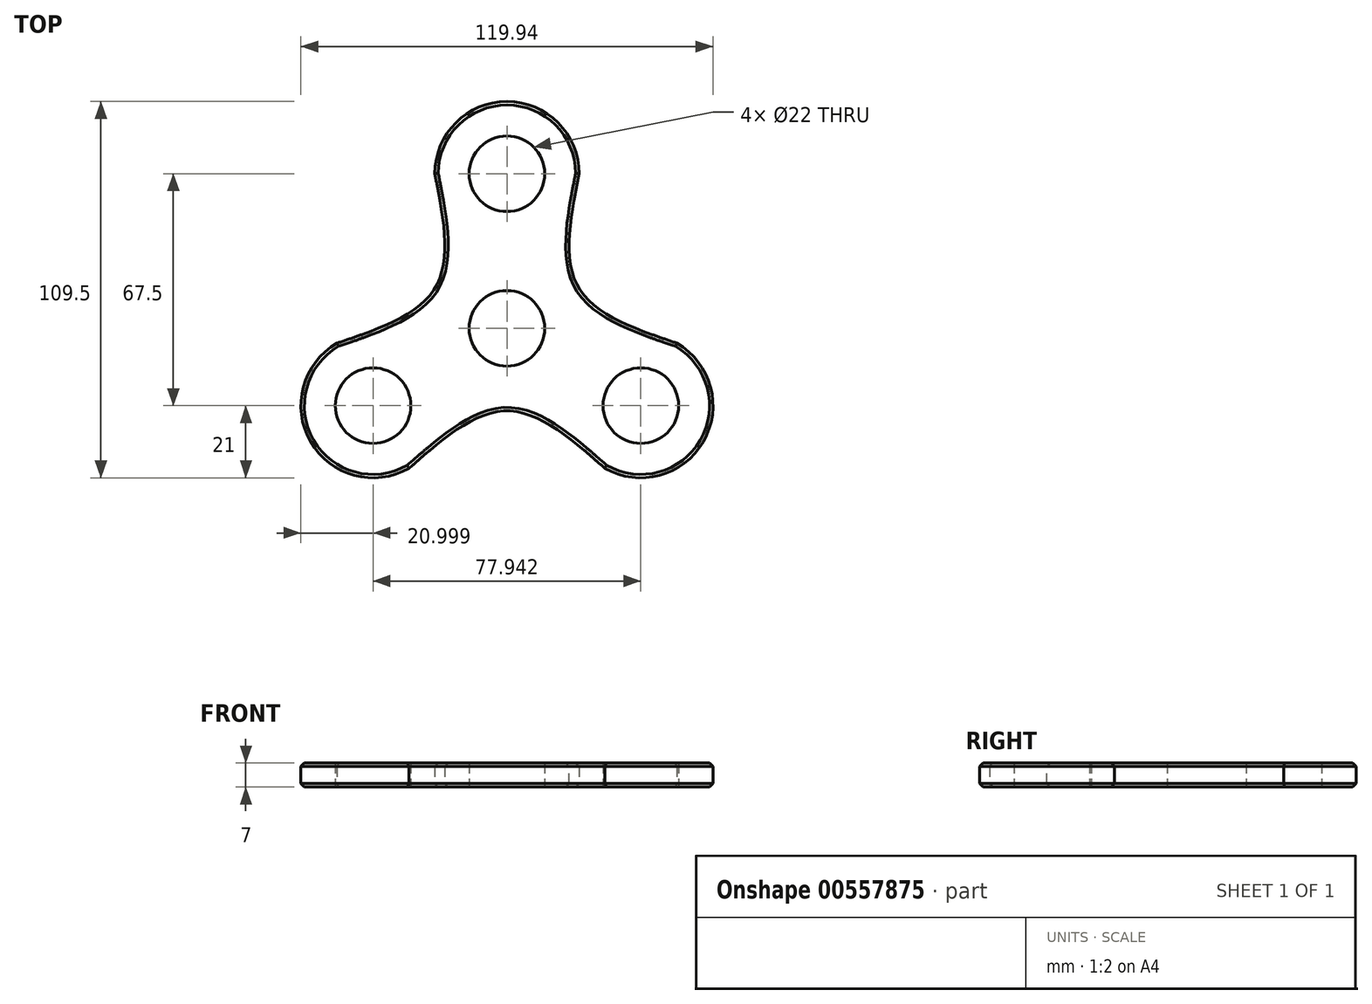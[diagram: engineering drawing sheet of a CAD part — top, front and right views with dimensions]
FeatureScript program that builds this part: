
annotation { "Feature Type Name" : "Feature", "Feature Type Description" : "" }
export const myFeature = defineFeature(function(context is Context, id is Id, definition is map)
    precondition{}
    {
        {
            var Q0;
            Q0=qCreatedBy(makeId("Top.planeOp"),FACE);
            var sketch = newSketch(context, id + "F0", { "sketchPlane" : qUnion([Q0])});
            skCircle(sketch, "E0", {"center": v(0, 0) * mm, "radius": 11 * mm});
            skLineSegment(sketch, "E1", {"start": v(0, 0) * mm, "end": v(0, 45) * mm, "construction": true});
            skLineSegment(sketch, "E2", {"start": v(0, 0) * mm, "end": v(38.97, -22.5) * mm, "construction": true});
            skLineSegment(sketch, "E3", {"start": v(0, 0) * mm, "end": v(-38.97, -22.5) * mm, "construction": true});
            skCircle(sketch, "E4", {"center": v(38.97, -22.5) * mm, "radius": 11 * mm});
            skCircle(sketch, "E5", {"center": v(0, 45) * mm, "radius": 11 * mm});
            skCircle(sketch, "E6", {"center": v(-38.97, -22.5) * mm, "radius": 11 * mm});
            skCircle(sketch, "E7", {"center": v(0, 0) * mm, "radius": 20 * mm});
            skArc(sketch, "E8", {"start": v(19.5, 37.2) * mm, "mid": v(0, 66) * mm, "end": v(-19.5, 37.2) * mm});
            skArc(sketch, "E9", {"start": v(22.47, -35.49) * mm, "mid": v(57.16, -33) * mm, "end": v(41.97, -1.72) * mm});
            skArc(sketch, "E10", {"start": v(-41.97, -1.72) * mm, "mid": v(-57.16, -33) * mm, "end": v(-22.47, -35.49) * mm});
            skLineSegment(sketch, "E11", {"start": v(38.97, -22.5) * mm, "end": v(0, 0) * mm, "construction": true});
            skLineSegment(sketch, "E12", {"start": v(-38.97, -22.5) * mm, "end": v(0, 0) * mm, "construction": true});
            skLineSegment(sketch, "E13", {"start": v(0, 0) * mm, "end": v(0, -45) * mm, "construction": true});
            skPoint(sketch, "E14", {"position": v(-21, 45) * mm});
            skPoint(sketch, "E15", {"position": v(-49.47, -4.31) * mm});
            skPoint(sketch, "E16", {"position": v(-28.47, -40.69) * mm});
            skPoint(sketch, "E17", {"position": v(49.47, -4.31) * mm});
            skPoint(sketch, "E18", {"position": v(28.47, -40.69) * mm});
            skPoint(sketch, "E19", {"position": v(-20.78, 12) * mm});
            skPoint(sketch, "E20", {"position": v(20.78, 12) * mm});
            skPoint(sketch, "E21", {"position": v(0, -24) * mm});
            skFitSpline(sketch, "E22", {"points": [v(-21, 45) * mm, v(-20.78, 12) * mm, v(-49.47, -4.31) * mm], "startDerivative": vector(14.88, -74.34) * mm, "endDerivative": vector(-71.82, -24.28) * mm});
            skFitSpline(sketch, "E23", {"points": [v(21, 45) * mm, v(20.78, 12) * mm, v(49.47, -4.31) * mm], "startDerivative": vector(-14.88, -74.34) * mm, "endDerivative": vector(71.82, -24.28) * mm});
            skFitSpline(sketch, "E24", {"points": [v(28.47, -40.69) * mm, v(0, -24) * mm, v(-28.47, -40.69) * mm], "startDerivative": vector(-56.94, 50.06) * mm, "endDerivative": vector(-56.94, -50.06) * mm});
            skPoint(sketch, "E25", {"position": v(-57.16, -33) * mm});
            skPoint(sketch, "E26", {"position": v(0, 66) * mm});
            skSolve(sketch);
        }
        {
            var Q0;
            Q0=makeQuery(id+"F0.imprint","IMPRINT",FACE,{"disambiguationData":[TD([[makeQuery(id+"F0.imprint","IMPRINT",EDGE,{"derivedFrom":sQuery(id+"F0.wireOp",EDGE,"E4")}),-1.0]])]});
            var Q1;
            Q1=makeQuery(id+"F0.imprint","IMPRINT",FACE,{"disambiguationData":[TD([[makeQuery(id+"F0.imprint","IMPRINT",EDGE,{"derivedFrom":sQuery(id+"F0.wireOp",EDGE,"E0")}),-1.0]])]});
            extrude(context, id + "F1", {"entities" : qUnion([Q0, Q1]), "depth" : 7 * mm, "offsetDistance" : 25 * mm});
        }
        {
            var Q0;
            Q0=makeQuery(id+"F1.opExtrude","CAP_EDGE",EDGE,{"disambiguationData":[OSD([sQuery(id+"F0.wireOp",EDGE,"E24")])],"isStart":true});
            var Q1;
            Q1=makeQuery(id+"F1.opExtrude","CAP_EDGE",EDGE,{"disambiguationData":[OSD([sQuery(id+"F0.wireOp",EDGE,"E22")])],"isStart":true});
            var Q2;
            Q2=makeQuery(id+"F1.opExtrude","CAP_EDGE",EDGE,{"disambiguationData":[OSD([sQuery(id+"F0.wireOp",EDGE,"E8")])],"isStart":true});
            var Q3;
            Q3=makeQuery(id+"F1.opExtrude","CAP_EDGE",EDGE,{"disambiguationData":[OSD([sQuery(id+"F0.wireOp",EDGE,"E23")])],"isStart":true});
            var Q4;
            Q4=makeQuery(id+"F1.opExtrude","CAP_EDGE",EDGE,{"disambiguationData":[OSD([sQuery(id+"F0.wireOp",EDGE,"E9")])],"isStart":true});
            var Q5;
            Q5=makeQuery(id+"F1.opExtrude","CAP_EDGE",EDGE,{"disambiguationData":[OSD([sQuery(id+"F0.wireOp",EDGE,"E10")])],"isStart":true});
            var Q6;
            Q6=makeQuery(id+"F1.opExtrude","CAP_EDGE",EDGE,{"disambiguationData":[OSD([sQuery(id+"F0.wireOp",EDGE,"E10")])],"isStart":false});
            var Q7;
            Q7=makeQuery(id+"F1.opExtrude","CAP_EDGE",EDGE,{"disambiguationData":[OSD([sQuery(id+"F0.wireOp",EDGE,"E22")])],"isStart":false});
            var Q8;
            Q8=makeQuery(id+"F1.opExtrude","CAP_EDGE",EDGE,{"disambiguationData":[OSD([sQuery(id+"F0.wireOp",EDGE,"E8")])],"isStart":false});
            var Q9;
            Q9=makeQuery(id+"F1.opExtrude","CAP_EDGE",EDGE,{"disambiguationData":[OSD([sQuery(id+"F0.wireOp",EDGE,"E23")])],"isStart":false});
            var Q10;
            Q10=makeQuery(id+"F1.opExtrude","CAP_EDGE",EDGE,{"disambiguationData":[OSD([sQuery(id+"F0.wireOp",EDGE,"E9")])],"isStart":false});
            var Q11;
            Q11=makeQuery(id+"F1.opExtrude","CAP_EDGE",EDGE,{"disambiguationData":[OSD([sQuery(id+"F0.wireOp",EDGE,"E24")])],"isStart":false});
            chamfer(context, id + "F2", {"entities" : qUnion([Q0, Q1, Q2, Q3, Q4, Q5, Q6, Q7, Q8, Q9, Q10, Q11]), "width" : 1 * mm, "tangentPropagation" : true});
        }
    });
